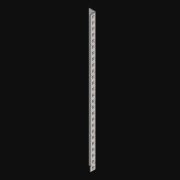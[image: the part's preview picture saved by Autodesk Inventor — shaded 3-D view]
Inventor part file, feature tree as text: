
AUTODESK INVENTOR PART (.ipt)
format: ipt  version: 2021 (Build 250183000, 183)  size: 1,269,760 bytes
history: native  units: in
note: dims shown in document units (in); Inventor stores cm internally (conversion verified against a paired STEP export)
features: extrude x54, other x52, sketch x4, pattern_linear x2, sheet_metal_op x1
ambient origin geometry x8: Origin, YZ Plane, XZ Plane, XY Plane, X Axis, Y Axis, Z Axis, Center Point
bodies: Solid1 (feature_tree)
feature tree (113):
  pattern_linear  "Rectangular Pattern1"  Spacing1=0.5in  [1 undecoded]
  pattern_linear  "Rectangular Pattern3"  Count1=26  [1 undecoded]
  extrude  "Extrusion1"  Depth=0.5in
  extrude  "Extrusion2"  Depth=0.5in
  sketch  "Sketch1"  dims[d0=0.182in]
  other  "Srf1"
  sketch  "Sketch3"  dims[d1=0.063in d2=0.0in]
  other  "Srf3"
  other  "Srf4"
  other  "Srf5"
  other  "Srf6"
  other  "Srf7"
  other  "Srf8"
  other  "Srf9"
  other  "Srf10"
  other  "Srf11"
  other  "Srf12"
  other  "Srf13"
  other  "Srf14"
  other  "Srf15"
  other  "Srf16"
  other  "Srf17"
  other  "Srf18"
  other  "Srf19"
  other  "Srf20"
  other  "Srf21"
  other  "Srf22"
  other  "Srf23"
  other  "Srf24"
  other  "Srf25"
  other  "Srf26"
  other  "Srf27"
  other  "Srf28"
  other  "Srf142"
  other  "Srf143"
  other  "Srf144"
  other  "Srf145"
  other  "Srf146"
  other  "Srf147"
  other  "Srf148"
  other  "Srf149"
  other  "Srf150"
  other  "Srf151"
  other  "Srf152"
  other  "Srf153"
  other  "Srf154"
  other  "Srf155"
  other  "Srf156"
  other  "Srf157"
  other  "Srf158"
  other  "Srf159"
  other  "Srf160"
  other  "Srf161"
  other  "Srf162"
  other  "Srf163"
  other  "Srf164"
  other  "Srf165"
  other  "Srf166"
  sketch  "Sketch4"  dims[d6=0.182in]
  sketch  "Sketch5"  dims[d7=0.063in d8=0.0in d11=0.5in d12=0.3937in d14=0.5in d18=10.2362in d20=0.5in d21=4.5in d22=0.0in d23=0.841in d24=0.0in]
  sheet_metal_op  "Fold1"
  extrude  "ExtrusionSrf1"  TaperAngle=0.0deg  [1 undecoded]
  extrude  "ExtrusionSrf3"  Depth=0.5in TaperAngle=0.0deg
  extrude  "ExtrusionSrf4"  [1 undecoded]
  extrude  "ExtrusionSrf5"  [1 undecoded]
  extrude  "ExtrusionSrf6"  [1 undecoded]
  extrude  "ExtrusionSrf7"  [1 undecoded]
  extrude  "ExtrusionSrf8"  [1 undecoded]
  extrude  "ExtrusionSrf9"  [1 undecoded]
  extrude  "ExtrusionSrf10"  [1 undecoded]
  extrude  "ExtrusionSrf11"  [1 undecoded]
  extrude  "ExtrusionSrf12"  [1 undecoded]
  extrude  "ExtrusionSrf13"  [1 undecoded]
  extrude  "ExtrusionSrf14"  [1 undecoded]
  extrude  "ExtrusionSrf15"  [1 undecoded]
  extrude  "ExtrusionSrf16"  [1 undecoded]
  extrude  "ExtrusionSrf17"  [1 undecoded]
  extrude  "ExtrusionSrf18"  [1 undecoded]
  extrude  "ExtrusionSrf19"  [1 undecoded]
  extrude  "ExtrusionSrf20"  [1 undecoded]
  extrude  "ExtrusionSrf21"  [1 undecoded]
  extrude  "ExtrusionSrf22"  [1 undecoded]
  extrude  "ExtrusionSrf23"  [1 undecoded]
  extrude  "ExtrusionSrf24"  [1 undecoded]
  extrude  "ExtrusionSrf25"  [1 undecoded]
  extrude  "ExtrusionSrf26"  [1 undecoded]
  extrude  "ExtrusionSrf27"  [1 undecoded]
  extrude  "ExtrusionSrf28"  [1 undecoded]
  extrude  "ExtrusionSrf142"  [1 undecoded]
  extrude  "ExtrusionSrf143"  [1 undecoded]
  extrude  "ExtrusionSrf144"  [1 undecoded]
  extrude  "ExtrusionSrf145"  [1 undecoded]
  extrude  "ExtrusionSrf146"  [1 undecoded]
  extrude  "ExtrusionSrf147"  [1 undecoded]
  extrude  "ExtrusionSrf148"  [1 undecoded]
  extrude  "ExtrusionSrf149"  [1 undecoded]
  extrude  "ExtrusionSrf150"  [1 undecoded]
  extrude  "ExtrusionSrf151"  [1 undecoded]
  extrude  "ExtrusionSrf152"  [1 undecoded]
  extrude  "ExtrusionSrf153"  [1 undecoded]
  extrude  "ExtrusionSrf154"  [1 undecoded]
  extrude  "ExtrusionSrf155"  [1 undecoded]
  extrude  "ExtrusionSrf156"  [1 undecoded]
  extrude  "ExtrusionSrf157"  [1 undecoded]
  extrude  "ExtrusionSrf158"  [1 undecoded]
  extrude  "ExtrusionSrf159"  [1 undecoded]
  extrude  "ExtrusionSrf160"  [1 undecoded]
  extrude  "ExtrusionSrf161"  [1 undecoded]
  extrude  "ExtrusionSrf162"  [1 undecoded]
  extrude  "ExtrusionSrf163"  [1 undecoded]
  extrude  "ExtrusionSrf164"  [1 undecoded]
  extrude  "ExtrusionSrf165"  [1 undecoded]
  extrude  "ExtrusionSrf166"  [1 undecoded]
note: 53 required parameter values undecoded (feature->parameter linkage not recoverable at this tier; creation-order binding heuristic only, values carry confidence <= 0.55)
